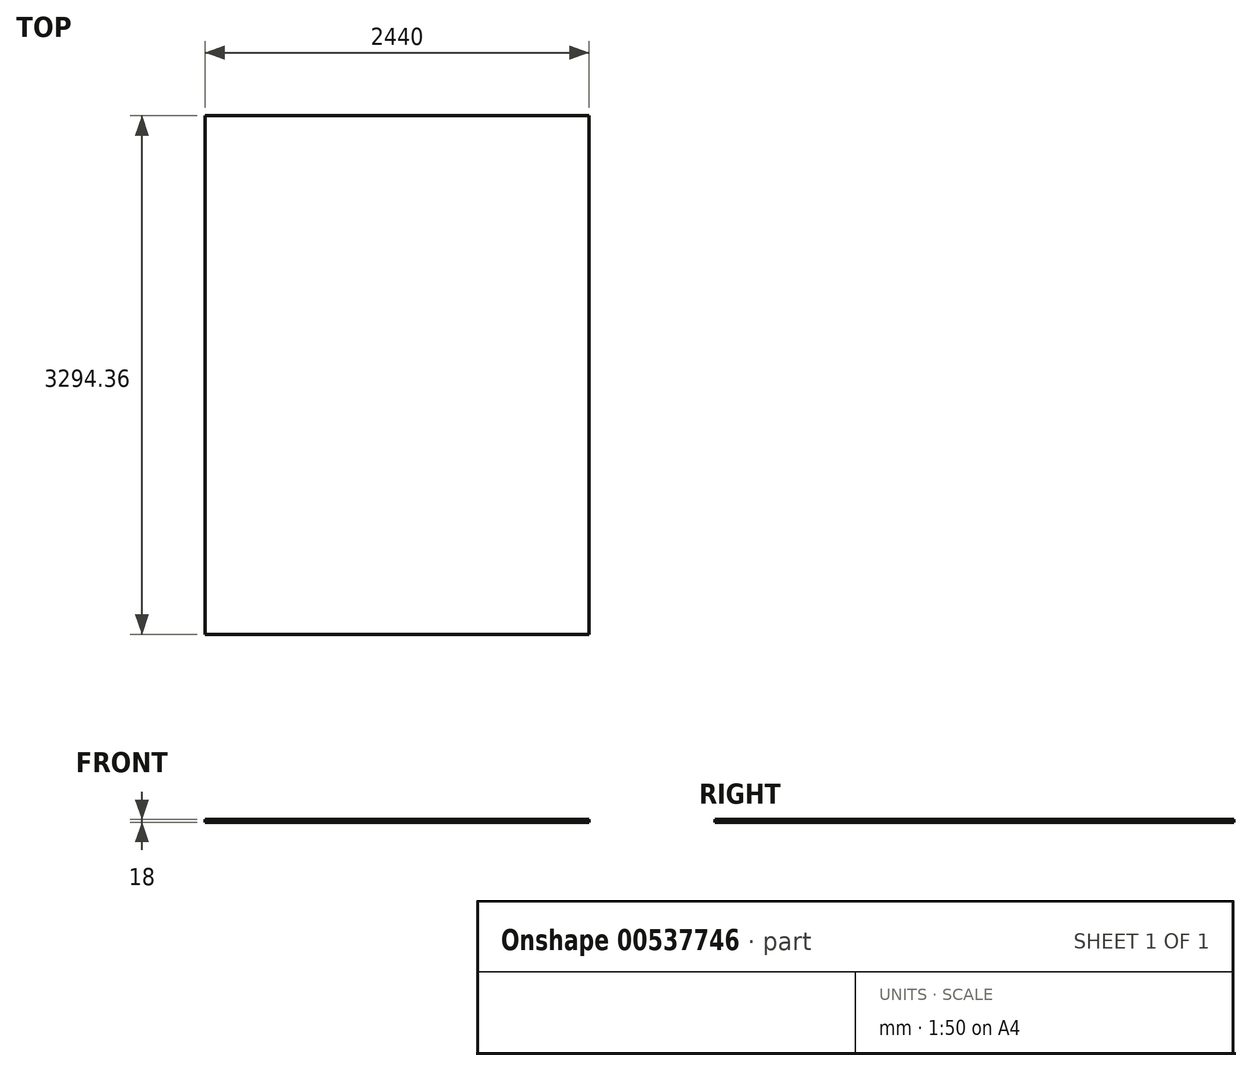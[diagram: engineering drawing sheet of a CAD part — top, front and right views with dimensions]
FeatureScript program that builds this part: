
annotation { "Feature Type Name" : "Feature", "Feature Type Description" : "" }
export const myFeature = defineFeature(function(context is Context, id is Id, definition is map)
    precondition{}
    {
        {
            var Q0;
            Q0=qCreatedBy(makeId("Top.planeOp"),FACE);
            var sketch = newSketch(context, id + "F0", { "sketchPlane" : qUnion([Q0])});
            skLineSegment(sketch, "E0.bottom", {"start": v(-901.16, 1652.95) * mm, "end": v(1538.84, 1652.95) * mm});
            skLineSegment(sketch, "E0.top", {"start": v(-901.16, -1641.4) * mm, "end": v(1538.84, -1641.4) * mm});
            skLineSegment(sketch, "E0.left", {"start": v(-901.16, 1652.95) * mm, "end": v(-901.16, -1641.4) * mm});
            skLineSegment(sketch, "E0.right", {"start": v(1538.84, 1652.95) * mm, "end": v(1538.84, -1641.4) * mm});
            skPoint(sketch, "E1.right.end.orphan", {"position": v(-1545.55, -1641.4) * mm});
            skSolve(sketch);
        }
        {
            var Q0;
            Q0 = qSketchRegion(id + "F0", true);
            extrude(context, id + "F1", {"entities" : qUnion([Q0]), "depth" : 18 * mm, "offsetDistance" : 25 * mm});
        }
    });
